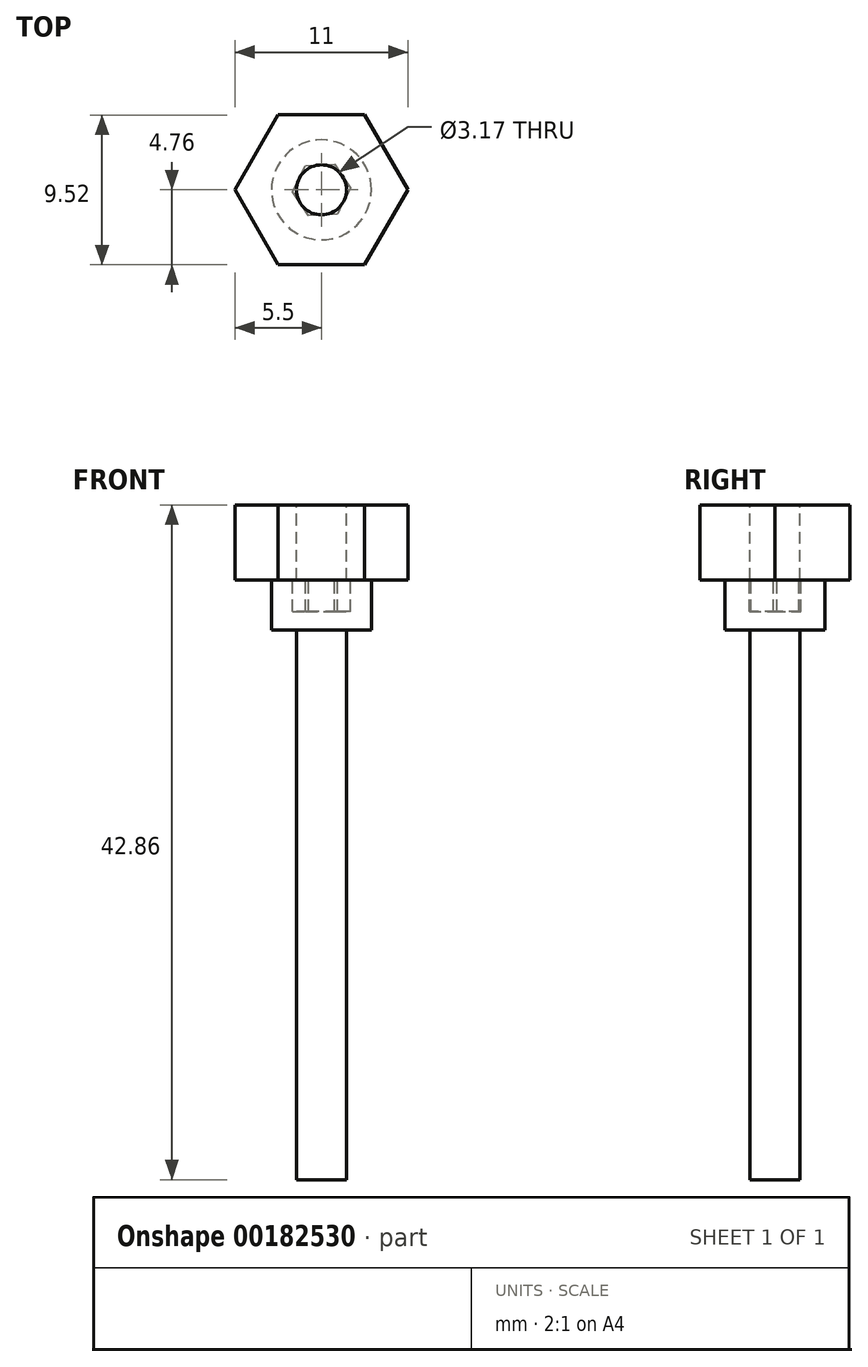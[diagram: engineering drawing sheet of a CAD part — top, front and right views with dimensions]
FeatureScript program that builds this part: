
annotation { "Feature Type Name" : "Feature", "Feature Type Description" : "" }
export const myFeature = defineFeature(function(context is Context, id is Id, definition is map)
    precondition{}
    {
        {
            var Q0;
            Q0=qCreatedBy(makeId("Top.planeOp"),FACE);
            var sketch = newSketch(context, id + "F0", { "sketchPlane" : qUnion([Q0])});
            skCircle(sketch, "E0.cCircle", {"center": v(0, 0) * mm, "radius": 4.76 * mm, "construction": true});
            skLineSegment(sketch, "E0.0", {"start": v(2.75, -4.76) * mm, "end": v(-2.75, -4.76) * mm});
            skLineSegment(sketch, "E0.1", {"start": v(-2.75, -4.76) * mm, "end": v(-5.5, 0) * mm});
            skLineSegment(sketch, "E0.2", {"start": v(-5.5, 0) * mm, "end": v(-2.75, 4.76) * mm});
            skLineSegment(sketch, "E0.3", {"start": v(-2.75, 4.76) * mm, "end": v(2.75, 4.76) * mm});
            skLineSegment(sketch, "E0.4", {"start": v(2.75, 4.76) * mm, "end": v(5.5, 0) * mm});
            skLineSegment(sketch, "E0.5", {"start": v(5.5, 0) * mm, "end": v(2.75, -4.76) * mm});
            skPoint(sketch, "E0.0.midPoint", {"position": v(0, -4.76) * mm});
            skSolve(sketch);
        }
        {
            var Q0;
            Q0 = qSketchRegion(id + "F0", true);
            extrude(context, id + "F1", {"entities" : qUnion([Q0]), "depth" : 4.76 * mm});
        }
        {
            var Q0;
            Q0=makeQuery(id+"F1.opExtrude","CAP_FACE",FACE,{"disambiguationData":[OSD([sQuery(id+"F0.wireOp",EDGE,"E0.0"),sQuery(id+"F0.wireOp",EDGE,"E0.1"),sQuery(id+"F0.wireOp",EDGE,"E0.2"),sQuery(id+"F0.wireOp",EDGE,"E0.3"),sQuery(id+"F0.wireOp",EDGE,"E0.4"),sQuery(id+"F0.wireOp",EDGE,"E0.5")])],"isStart":false});
            var sketch = newSketch(context, id + "F2", { "sketchPlane" : qUnion([Q0])});
            skCircle(sketch, "E1", {"center": v(0, 0) * mm, "radius": 2.95 * mm});
            skSolve(sketch);
        }
        {
            var Q0;
            Q0=sQuery(id+"F2.wireOp",VERTEX,"E1.center");
            var Q1;
            Q1=makeQuery(id+"F1.opExtrude","SWEPT_BODY",BODY,{"disambiguationData":[OSD([sQuery(id+"F0.wireOp",EDGE,"E0.0"),sQuery(id+"F0.wireOp",EDGE,"E0.1"),sQuery(id+"F0.wireOp",EDGE,"E0.2"),sQuery(id+"F0.wireOp",EDGE,"E0.3"),sQuery(id+"F0.wireOp",EDGE,"E0.4"),sQuery(id+"F0.wireOp",EDGE,"E0.5")])]});
            hole(context, id + "F3", {"style" : HoleStyle.SIMPLE, "endStyle" : HoleEndStyle.THROUGH, "holeDiameter" : 3.17 * mm, "startFromSketch" : true, "locations" : qUnion([Q0]), "scope" : qUnion([Q1]), "isTappedThrough" : true});
        }
        {
            var Q0;
            Q0=qCreatedBy(makeId("Top.planeOp"),FACE);
            var sketch = newSketch(context, id + "F4", { "sketchPlane" : qUnion([Q0])});
            skCircle(sketch, "E2", {"center": v(0, 0) * mm, "radius": 3.18 * mm});
            skSolve(sketch);
        }
        {
            var Q0;
            Q0=makeQuery(id+"F4.imprint","IMPRINT",FACE,{"disambiguationData":[TD([[makeQuery(id+"F4.imprint","IMPRINT",EDGE,{"derivedFrom":sQuery(id+"F4.wireOp",EDGE,"E2")}),1.0]])]});
            extrude(context, id + "F5", {"entities" : qUnion([Q0]), "oppositeDirection" : true, "depth" : 3.17 * mm});
        }
        {
            var Q0;
            Q0=makeQuery(id+"F5.opExtrude","CAP_FACE",FACE,{"disambiguationData":[OSD([sQuery(id+"F4.wireOp",EDGE,"E2")])],"isStart":false});
            var sketch = newSketch(context, id + "F6", { "sketchPlane" : qUnion([Q0])});
            skSolve(sketch);
        }
        {
            var Q0;
            Q0=makeQuery(id+"F6.imprint","IMPRINT",FACE,{"disambiguationData":[TD([[makeQuery(id+"F6.imprint","IMPRINT",EDGE,{"derivedFrom":makeQuery(id+"F5.opExtrude","CAP_EDGE",EDGE,{"disambiguationData":[OSD([sQuery(id+"F4.wireOp",EDGE,"E2")])],"isStart":false})}),-1.0]])]});
            var sketch = newSketch(context, id + "F7", { "sketchPlane" : qUnion([Q0])});
            skCircle(sketch, "E3", {"center": v(0, 0) * mm, "radius": 1.59 * mm});
            skSolve(sketch);
        }
        {
            var Q0;
            Q0 = qSketchRegion(id + "F7", true);
            extrude(context, id + "F8", {"entities" : qUnion([Q0]), "operationType" : NewBodyOperationType.ADD, "depth" : 34.92 * mm});
        }
        {
            var Q0;
            Q0=qCreatedBy(makeId("Top.planeOp"),FACE);
            var sketch = newSketch(context, id + "F9", { "sketchPlane" : qUnion([Q0])});
            skCircle(sketch, "E4.cCircle", {"center": v(0, 0) * mm, "radius": 1.59 * mm, "construction": true});
            skLineSegment(sketch, "E4.0", {"start": v(0.82, 1.64) * mm, "end": v(1.83, 0.1) * mm});
            skLineSegment(sketch, "E4.1", {"start": v(1.83, 0.1) * mm, "end": v(1, -1.53) * mm});
            skLineSegment(sketch, "E4.2", {"start": v(1, -1.53) * mm, "end": v(-0.82, -1.64) * mm});
            skLineSegment(sketch, "E4.3", {"start": v(-0.82, -1.64) * mm, "end": v(-1.83, -0.1) * mm});
            skLineSegment(sketch, "E4.4", {"start": v(-1.83, -0.1) * mm, "end": v(-1, 1.53) * mm});
            skLineSegment(sketch, "E4.5", {"start": v(-1, 1.53) * mm, "end": v(0.82, 1.64) * mm});
            skPoint(sketch, "E4.0.midPoint", {"position": v(1.33, 0.87) * mm});
            skSolve(sketch);
        }
        {
            var Q0;
            Q0 = qSketchRegion(id + "F9", true);
            extrude(context, id + "F10", {"entities" : qUnion([Q0]), "operationType" : NewBodyOperationType.REMOVE, "oppositeDirection" : true, "depth" : 2 * mm});
        }
    });
